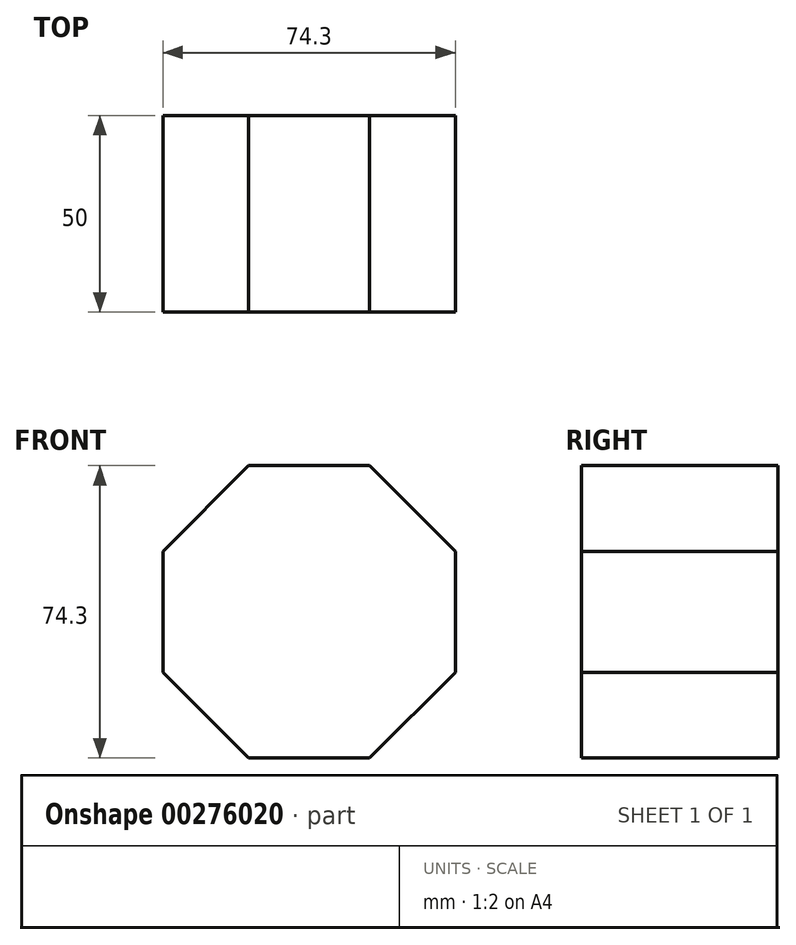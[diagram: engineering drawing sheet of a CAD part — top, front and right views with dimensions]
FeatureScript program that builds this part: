
annotation { "Feature Type Name" : "Feature", "Feature Type Description" : "" }
export const myFeature = defineFeature(function(context is Context, id is Id, definition is map)
    precondition{}
    {
        {
            var Q0;
            Q0=qCreatedBy(makeId("Front.planeOp"),FACE);
            var sketch = newSketch(context, id + "F0", { "sketchPlane" : qUnion([Q0])});
            skCircle(sketch, "E0.cCircle", {"center": v(0, 0) * mm, "radius": 37.15 * mm, "construction": true});
            skLineSegment(sketch, "E0.0", {"start": v(-15.39, 37.15) * mm, "end": v(15.39, 37.15) * mm});
            skLineSegment(sketch, "E0.1", {"start": v(15.39, 37.15) * mm, "end": v(37.15, 15.39) * mm});
            skLineSegment(sketch, "E0.2", {"start": v(37.15, 15.39) * mm, "end": v(37.15, -15.39) * mm});
            skLineSegment(sketch, "E0.3", {"start": v(37.15, -15.39) * mm, "end": v(15.39, -37.15) * mm});
            skLineSegment(sketch, "E0.4", {"start": v(15.39, -37.15) * mm, "end": v(-15.39, -37.15) * mm});
            skLineSegment(sketch, "E0.5", {"start": v(-15.39, -37.15) * mm, "end": v(-37.15, -15.39) * mm});
            skLineSegment(sketch, "E0.6", {"start": v(-37.15, -15.39) * mm, "end": v(-37.15, 15.39) * mm});
            skLineSegment(sketch, "E0.7", {"start": v(-37.15, 15.39) * mm, "end": v(-15.39, 37.15) * mm});
            skPoint(sketch, "E0.0.midPoint", {"position": v(0, 37.15) * mm});
            skSolve(sketch);
        }
        {
            var Q0;
            Q0=qCreatedBy(makeId("Front.planeOp"),FACE);
            cPlane(context, id + "F1", {"entities" : qUnion([Q0]), "cplaneType" : CPlaneType.OFFSET, "offset" : 50 * mm, "width" : 150 * mm, "height" : 150 * mm});
        }
        {
            var Q0;
            Q0=qCreatedBy(id+"F1.planeOp",FACE);
            var sketch = newSketch(context, id + "F2", { "sketchPlane" : qUnion([Q0])});
            skCircle(sketch, "E1.cCircle", {"center": v(0, 0) * mm, "radius": 37.15 * mm, "construction": true});
            skLineSegment(sketch, "E1.0", {"start": v(-15.39, 37.15) * mm, "end": v(15.39, 37.15) * mm});
            skLineSegment(sketch, "E1.1", {"start": v(15.39, 37.15) * mm, "end": v(37.15, 15.39) * mm});
            skLineSegment(sketch, "E1.2", {"start": v(37.15, 15.39) * mm, "end": v(37.15, -15.39) * mm});
            skLineSegment(sketch, "E1.3", {"start": v(37.15, -15.39) * mm, "end": v(15.39, -37.15) * mm});
            skLineSegment(sketch, "E1.4", {"start": v(15.39, -37.15) * mm, "end": v(-15.39, -37.15) * mm});
            skLineSegment(sketch, "E1.5", {"start": v(-15.39, -37.15) * mm, "end": v(-37.15, -15.39) * mm});
            skLineSegment(sketch, "E1.6", {"start": v(-37.15, -15.39) * mm, "end": v(-37.15, 15.39) * mm});
            skLineSegment(sketch, "E1.7", {"start": v(-37.15, 15.39) * mm, "end": v(-15.39, 37.15) * mm});
            skPoint(sketch, "E1.0.midPoint", {"position": v(0, 37.15) * mm});
            skSolve(sketch);
        }
        {
            var Q0;
            Q0=makeQuery(id+"F0.imprint","IMPRINT",FACE,{"disambiguationData":[TD([[makeQuery(id+"F0.imprint","IMPRINT",EDGE,{"derivedFrom":sQuery(id+"F0.wireOp",EDGE,"E0.0")}),-1.0]])]});
            var Q1;
            Q1=makeQuery(id+"F2.imprint","IMPRINT",FACE,{"disambiguationData":[TD([[makeQuery(id+"F2.imprint","IMPRINT",EDGE,{"derivedFrom":sQuery(id+"F2.wireOp",EDGE,"E1.0")}),-1.0]])]});
            loft(context, id + "F3", {"sheetProfilesArray" : [{ "sheetProfileEntities" : qUnion([Q0]) }, { "sheetProfileEntities" : qUnion([Q1]) }]});
        }
    });
